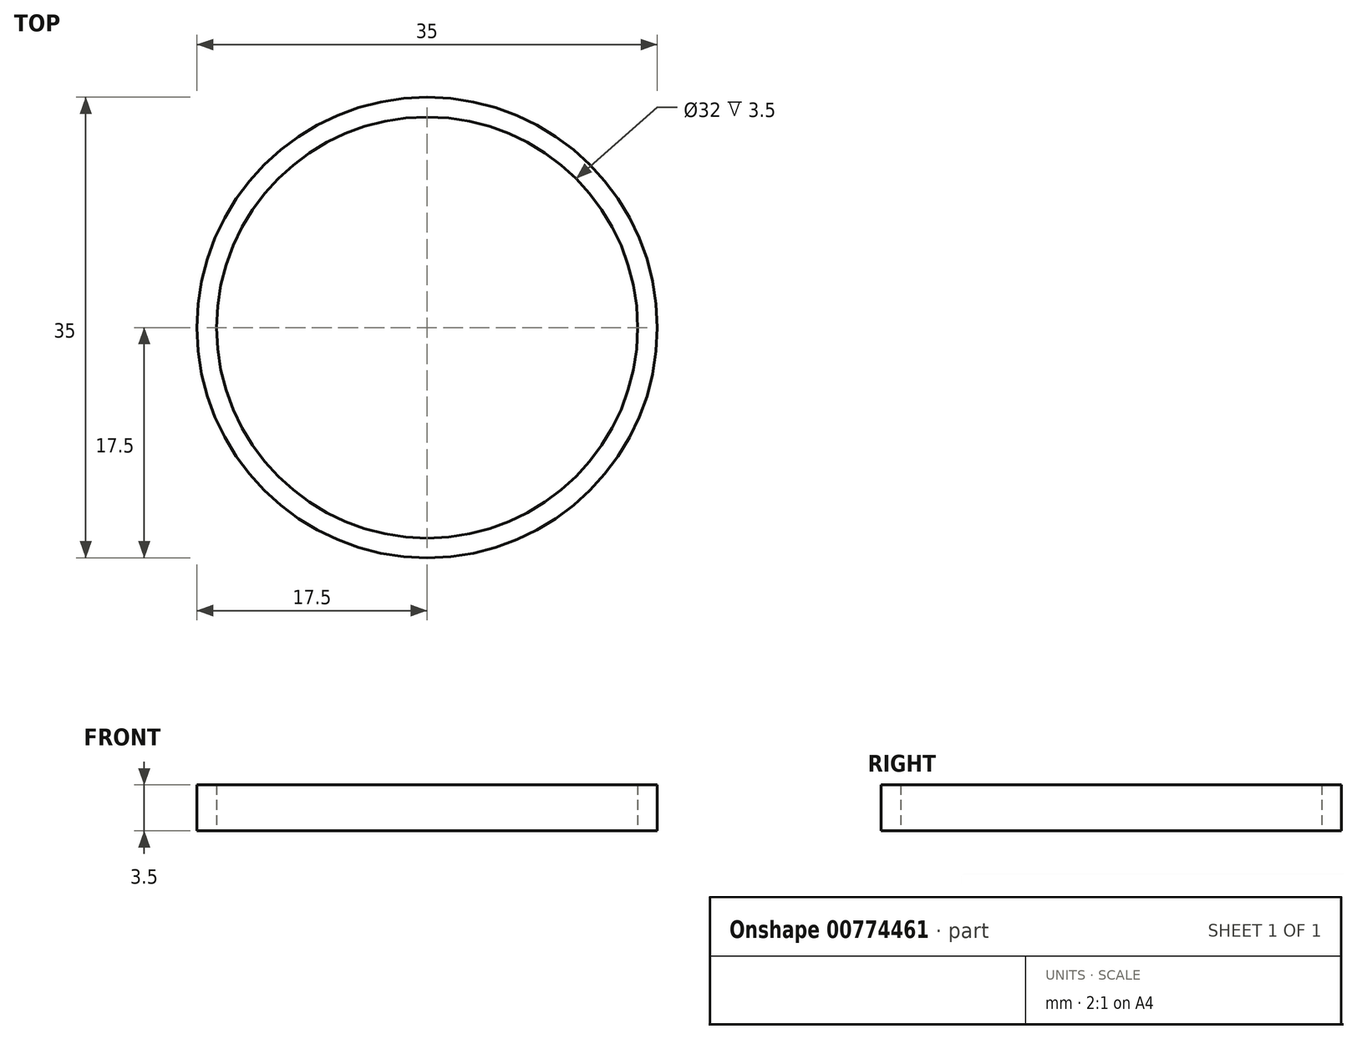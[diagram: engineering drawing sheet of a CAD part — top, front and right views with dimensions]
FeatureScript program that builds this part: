
annotation { "Feature Type Name" : "Feature", "Feature Type Description" : "" }
export const myFeature = defineFeature(function(context is Context, id is Id, definition is map)
    precondition{}
    {
        {
            var Q0;
            Q0=qCreatedBy(makeId("Top.planeOp"),FACE);
            var sketch = newSketch(context, id + "F0", { "sketchPlane" : qUnion([Q0])});
            skCircle(sketch, "E0", {"center": v(0, 0) * mm, "radius": 17.5 * mm});
            skCircle(sketch, "E1", {"center": v(0, 0) * mm, "radius": 16 * mm});
            skSolve(sketch);
        }
        {
            var Q0;
            Q0 = qSketchRegion(id + "F0", true);
            extrude(context, id + "F1", {"entities" : qUnion([Q0]), "depth" : 3.5 * mm, "offsetDistance" : 25 * mm});
        }
    });
